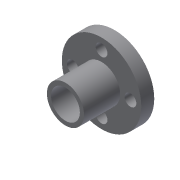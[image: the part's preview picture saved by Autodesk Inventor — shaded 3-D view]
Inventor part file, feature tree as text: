
AUTODESK INVENTOR PART (.ipt)
format: ipt  version: 2019.4 (Build 234330000, 330)  size: 114,176 bytes
history: native  units: mm
features: extrude x3, sketch x3, projected_geometry x2, pattern_circular x1
ambient origin geometry x8: Origin, YZ Plane, XZ Plane, XY Plane, X Axis, Y Axis, Z Axis, Center Point
bodies: Solid1 (feature_tree)
feature tree (9):
  extrude  "Extrusion1"  Depth=22.0mm
  extrude  "Extrusion2"  Depth=3.6mm
  extrude  "Extrusion3"  Depth=10.0mm
  pattern_circular  "Circular Pattern1"  [2 undecoded]
  sketch  "Sketch1"  dims[d0=8.0mm d1=22.0mm]
  sketch  "Sketch2"  dims[d2=3.6mm d3=0.0mm d4=10.3mm]
  projected_geometry  "Projected Loop1"
  sketch  "Sketch3"  dims[d5=10.0mm d6=0.0mm d7=3.25mm d8=8.0mm d9=10.0mm d10=0.0mm d11=40.0mm d12=360.0deg]
  projected_geometry  "Projected Loop2"
note: 2 required parameter values undecoded (feature->parameter linkage not recoverable at this tier; creation-order binding heuristic only, values carry confidence <= 0.55)
